# Revit family: equip-water-cooler-elkay-erfp-bi-level
name_source: partatom
category: Plumbing Fixtures
units: mm (PartAtom-declared; Revit-internal decimal feet)

## family parameters
Always vertical = Yes
Cut with Voids When Loaded = No
OmniClass Number = 23.45.00.00
OmniClass Title = Sanitary, Laundry, and Cleaning Equipment
Part Type = Normal
Room Calculation Point = No
Round Connector Dimension = Use Radius
Shared = No
Work Plane-Based = No

## types (5) — shared parameters
Basin Material = Metal - Steel - Stainless - Chrome
Bubbler = Flexi-Guard
Button Material = Metal - Steel - Stainless - Chrome
CW Connection = Yes
Chiller = ECH82
Cooler Depth = 1' - 6 5/8"
Cooler Separation = 0' - 6 5/8"
Cooler Width = 1' - 0 1/8"
Description = Water Cooler
Dispenser Height = 2' - 9"
HW Connection = No
Lower Cooler Rim Height = 2' - 9 1/2"
Lower Orifice Height = 2' - 11 1/8"
Manufacturer = Elkay
Orifice to Rim = 0' - 1 5/8"
Panel Material = Metal - Steel - Stainless - Chrome
Rim to Dispenser = 0' - 6 1/2"
Type = Bi-level (High-Low)
URL = http://www.elkay.com
Upper Cooler Depth = 1' - 0 7/8"
Upper Cooler Rim Height = 3' - 3 1/2"
Upper Orifice Height = 3' - 5 1/8"
Upper Rim Height = 3' - 3 1/2"
Vent Connection = No
Version = 1.0.0.0
Volts/Hertz = 220V/50Hz
Wall Plate Material = Metal - Steel - Stainless - Chrome
Waste Connection = Yes
Water Service Flow = 0 GPM
Water Service Size Radius = 0' - 0 1/4"

## per-type parameters (varying)
| type | Activation | Filter | Fountian | Mounting |
| ERFPM282K | Pushbutton | See LNTEM82K | ERFPD282C | MF200 |
| ERFP282K | Pushbutton | See LNTE82K | ERFPD282C | ***Order MF200 Sparately |
| EROM282K | Sensor | ***ACC (EWF172) | EROD282C | MF200 |
| LNTEM82K | Pushbutton | EWF172 | LNTED82C | MF200 |
| LNTE82K | Pushbutton | EWF172 | LNTED82C | ***Order MF200 Sparately |

note: column(s) folded — value = type name in every type: Model

## geometry (parser evidence)
native form markers: Sweep x7
no freeform markers — native parametric forms only
